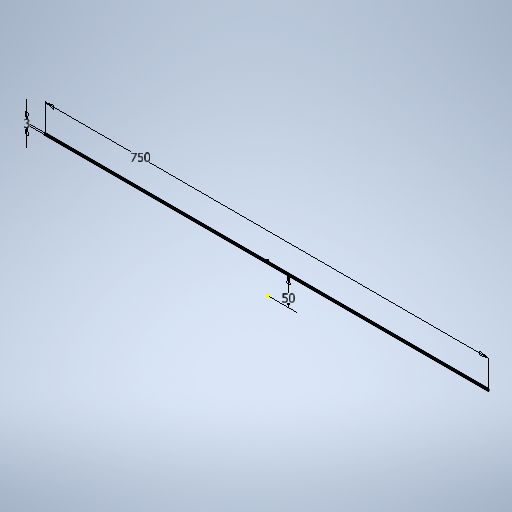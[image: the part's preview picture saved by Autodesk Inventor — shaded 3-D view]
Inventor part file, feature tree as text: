
AUTODESK INVENTOR PART (.ipt)
format: ipt  version: 2025.2 (Build 292293000, 293)  size: 233,984 bytes
history: native  units: mm
features: sketch x1
ambient origin geometry x8: Origin, YZ Plane, XZ Plane, XY Plane, X Axis, Y Axis, Z Axis, Center Point
feature tree (1):
  sketch  "Esboço1"  dims[d0=750.0mm d1=50.0mm d2=3.0mm]
